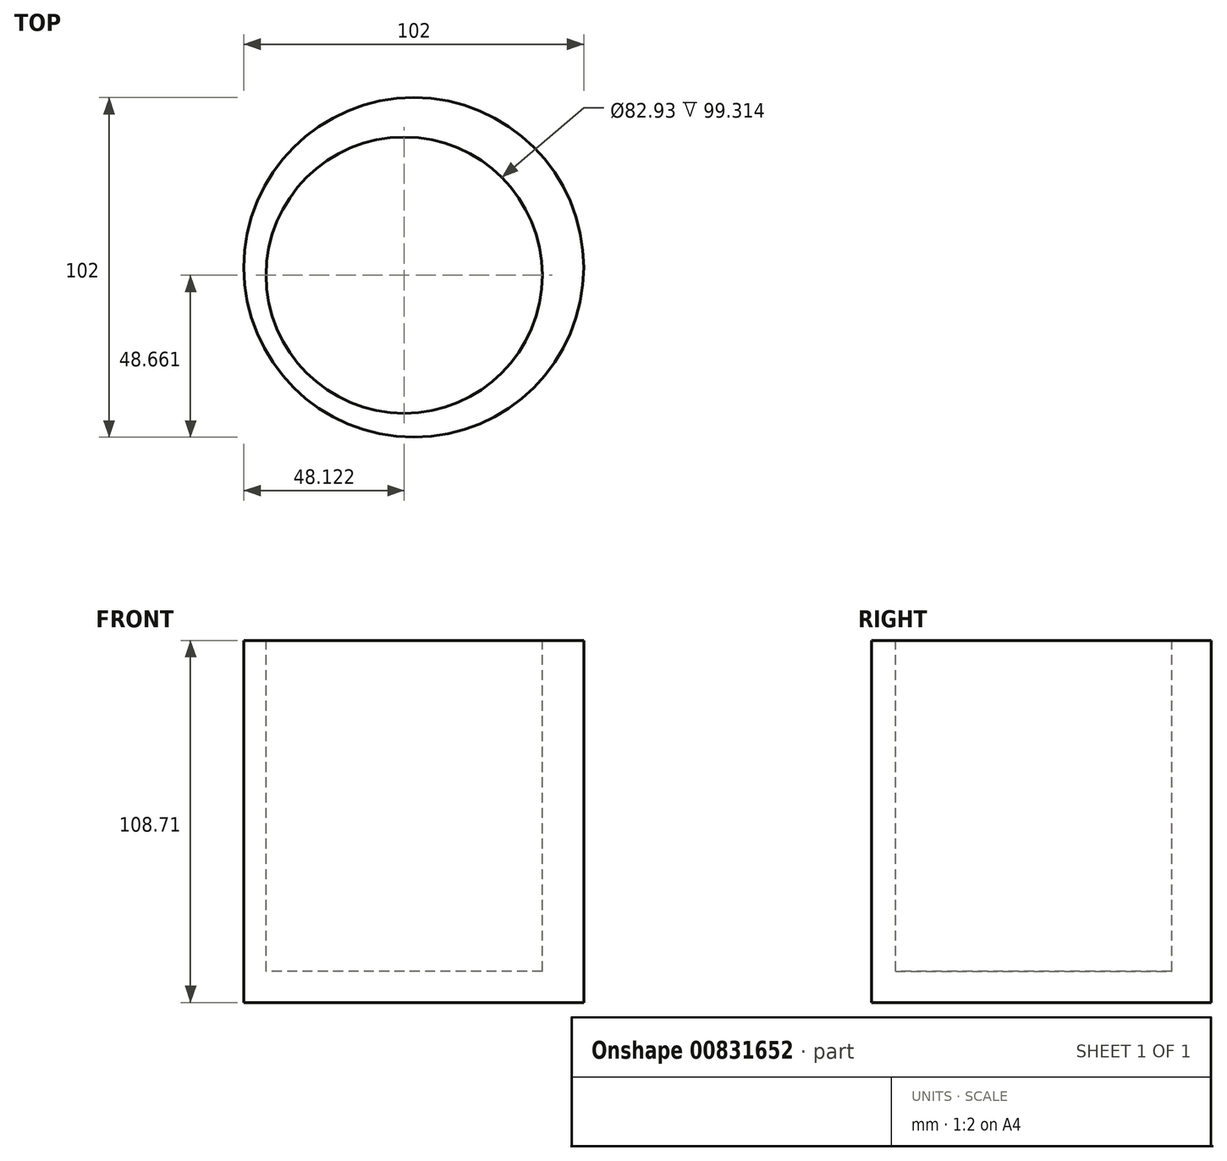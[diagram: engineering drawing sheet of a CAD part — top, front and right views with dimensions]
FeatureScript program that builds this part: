
annotation { "Feature Type Name" : "Feature", "Feature Type Description" : "" }
export const myFeature = defineFeature(function(context is Context, id is Id, definition is map)
    precondition{}
    {
        {
            var Q0;
            Q0=qCreatedBy(makeId("Top.planeOp"),FACE);
            var sketch = newSketch(context, id + "F0", { "sketchPlane" : qUnion([Q0])});
            skCircle(sketch, "E0", {"center": v(-14.92, 41.69) * mm, "radius": 10.46 * mm});
            skCircle(sketch, "E1", {"center": v(-55.3, 38.02) * mm, "radius": 51 * mm});
            skSolve(sketch);
        }
        {
            var Q0;
            Q0=makeQuery(id+"F0.imprint","IMPRINT",FACE,{"disambiguationData":[TD([[makeQuery(id+"F0.imprint","IMPRINT",EDGE,{"derivedFrom":sQuery(id+"F0.wireOp",EDGE,"E0")}),1.0]])]});
            var Q1;
            Q1=makeQuery(id+"F0.imprint","IMPRINT",FACE,{"disambiguationData":[TD([[makeQuery(id+"F0.imprint","IMPRINT",EDGE,{"derivedFrom":sQuery(id+"F0.wireOp",EDGE,"E0")}),-1.0]])]});
            var Q2;
            Q2=sQuery(id+"F0.wireOp",EDGE,"E1");
            extrude(context, id + "F1", {"entities" : qUnion([Q0, Q1]), "surfaceEntities" : qUnion([Q2]), "oppositeDirection" : true, "depth" : 108.7 * mm, "offsetDistance" : 25.4 * mm});
        }
        {
            var Q0;
            Q0=qCreatedBy(makeId("Top.planeOp"),FACE);
            var sketch = newSketch(context, id + "F2", { "sketchPlane" : qUnion([Q0])});
            skCircle(sketch, "E2", {"center": v(-58.17, 35.68) * mm, "radius": 41.47 * mm});
            skSolve(sketch);
        }
        {
            var Q0;
            Q0=makeQuery(id+"F2.imprint","IMPRINT",FACE,{"disambiguationData":[TD([[makeQuery(id+"F2.imprint","IMPRINT",EDGE,{"derivedFrom":sQuery(id+"F2.wireOp",EDGE,"E2")}),1.0]])]});
            var Q1;
            Q1=sQuery(id+"F2.wireOp",EDGE,"E2");
            extrude(context, id + "F3", {"entities" : qUnion([Q0]), "operationType" : NewBodyOperationType.REMOVE, "surfaceEntities" : qUnion([Q1]), "oppositeDirection" : true, "depth" : 99.31 * mm, "offsetDistance" : 25.4 * mm});
        }
    });
